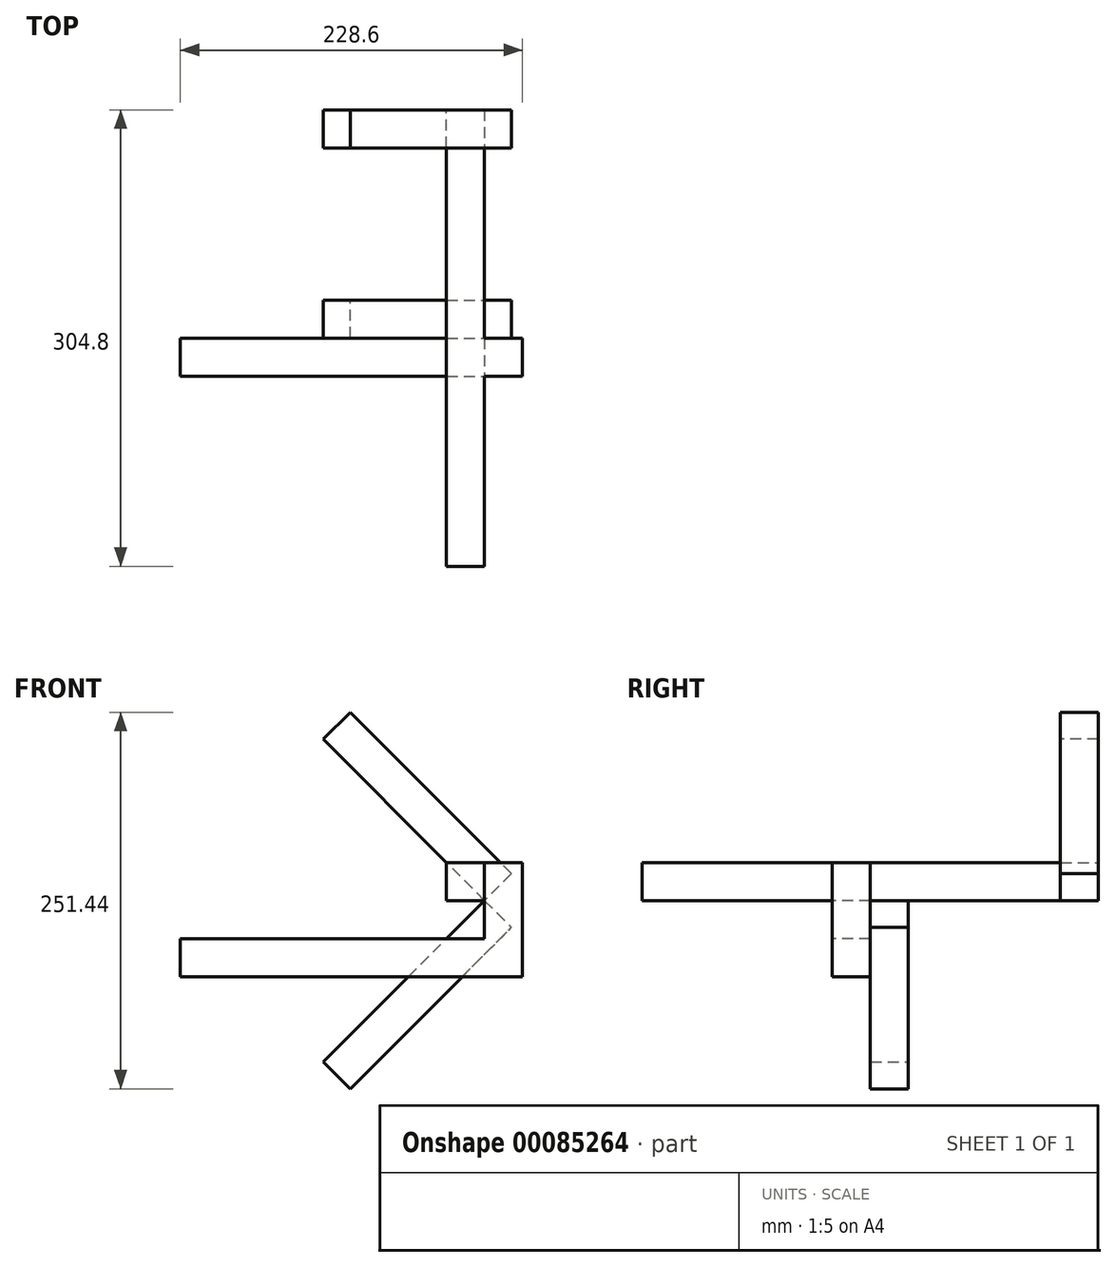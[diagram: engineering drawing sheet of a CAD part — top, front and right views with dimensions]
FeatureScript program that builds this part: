
annotation { "Feature Type Name" : "Feature", "Feature Type Description" : "" }
export const myFeature = defineFeature(function(context is Context, id is Id, definition is map)
    precondition{}
    {
        {
            var Q0;
            Q0=qCreatedBy(makeId("Front.planeOp"),FACE);
            var sketch = newSketch(context, id + "F0", { "sketchPlane" : qUnion([Q0])});
            skLineSegment(sketch, "E0.bottom", {"start": v(0, 0) * mm, "end": v(-25.4, 0) * mm});
            skLineSegment(sketch, "E0.top", {"start": v(0, 25.4) * mm, "end": v(-25.4, 25.4) * mm});
            skLineSegment(sketch, "E0.left", {"start": v(0, 0) * mm, "end": v(0, 25.4) * mm});
            skLineSegment(sketch, "E0.right", {"start": v(-25.4, 0) * mm, "end": v(-25.4, 25.4) * mm});
            skSolve(sketch);
        }
        {
            var Q0;
            Q0=makeQuery(id+"F0.imprint","IMPRINT",FACE,{"disambiguationData":[TD([[makeQuery(id+"F0.imprint","IMPRINT",EDGE,{"derivedFrom":sQuery(id+"F0.wireOp",EDGE,"E0.bottom")}),-1.0]])]});
            extrude(context, id + "F1", {"entities" : qUnion([Q0]), "endBound" : BoundingType.SYMMETRIC, "depth" : 304.8 * mm});
        }
        {
            var Q0;
            Q0=qCreatedBy(makeId("Top.planeOp"),FACE);
            var sketch = newSketch(context, id + "F2", { "sketchPlane" : qUnion([Q0])});
            skLineSegment(sketch, "E1.bottom", {"start": v(0, 0) * mm, "end": v(25.4, 0) * mm});
            skLineSegment(sketch, "E1.top", {"start": v(0, -25.4) * mm, "end": v(25.4, -25.4) * mm});
            skLineSegment(sketch, "E1.left", {"start": v(0, 0) * mm, "end": v(0, -25.4) * mm});
            skLineSegment(sketch, "E1.right", {"start": v(25.4, 0) * mm, "end": v(25.4, -25.4) * mm});
            skSolve(sketch);
        }
        {
            var Q0;
            Q0=makeQuery(id+"F2.imprint","IMPRINT",FACE,{"disambiguationData":[TD([[makeQuery(id+"F2.imprint","IMPRINT",EDGE,{"derivedFrom":sQuery(id+"F2.wireOp",EDGE,"E1.bottom")}),-1.0]])]});
            extrude(context, id + "F3", {"entities" : qUnion([Q0]), "operationType" : NewBodyOperationType.ADD, "depth" : 25.4 * mm});
        }
        {
            var Q0;
            Q0=makeQuery(id+"F2.imprint","IMPRINT",FACE,{"disambiguationData":[TD([[makeQuery(id+"F2.imprint","IMPRINT",EDGE,{"derivedFrom":sQuery(id+"F2.wireOp",EDGE,"E1.bottom")}),-1.0]])]});
            extrude(context, id + "F4", {"entities" : qUnion([Q0]), "operationType" : NewBodyOperationType.ADD, "oppositeDirection" : true, "depth" : 50.8 * mm});
        }
        {
            var Q0;
            Q0=qCreatedBy(makeId("Right.planeOp"),FACE);
            var sketch = newSketch(context, id + "F5", { "sketchPlane" : qUnion([Q0])});
            skLineSegment(sketch, "E2.0.0", {"start": v(-25.4, 0) * mm, "end": v(0, 0) * mm});
            skLineSegment(sketch, "E2.0.1", {"start": v(0, 0) * mm, "end": v(0, -50.8) * mm});
            skLineSegment(sketch, "E2.0.2", {"start": v(0, -50.8) * mm, "end": v(-25.4, -50.8) * mm});
            skLineSegment(sketch, "E2.0.3", {"start": v(-25.4, -50.8) * mm, "end": v(-25.4, 0) * mm});
            skLineSegment(sketch, "E3.top", {"start": v(0, -25.4) * mm, "end": v(-25.4, -25.4) * mm});
            skLineSegment(sketch, "E3.left", {"start": v(0, -50.8) * mm, "end": v(0, -25.4) * mm});
            skLineSegment(sketch, "E3.right", {"start": v(-25.4, -50.8) * mm, "end": v(-25.4, -25.4) * mm});
            skSolve(sketch);
        }
        {
            var Q0;
            Q0=makeQuery(id+"F5.imprint","IMPRINT",FACE,{"disambiguationData":[TD([[makeQuery(id+"F5.imprint","IMPRINT",EDGE,{"derivedFrom":sQuery(id+"F5.wireOp",EDGE,"E2.0.2")}),-1.0]])]});
            extrude(context, id + "F6", {"entities" : qUnion([Q0]), "operationType" : NewBodyOperationType.ADD, "oppositeDirection" : true, "depth" : 203.2 * mm});
        }
        {
            var Q0;
            Q0=qCreatedBy(makeId("Top.planeOp"),FACE);
            var sketch = newSketch(context, id + "F7", { "sketchPlane" : qUnion([Q0])});
            skLineSegment(sketch, "E4.bottom", {"start": v(0, 0) * mm, "end": v(25.4, 0) * mm});
            skLineSegment(sketch, "E4.top", {"start": v(0, 25.4) * mm, "end": v(25.4, 25.4) * mm});
            skLineSegment(sketch, "E4.left", {"start": v(0, 0) * mm, "end": v(0, 25.4) * mm});
            skLineSegment(sketch, "E4.right", {"start": v(25.4, 0) * mm, "end": v(25.4, 25.4) * mm});
            skSolve(sketch);
        }
        {
            var Q0;
            Q0=makeQuery(id+"F7.imprint","IMPRINT",FACE,{"disambiguationData":[TD([[makeQuery(id+"F7.imprint","IMPRINT",EDGE,{"derivedFrom":sQuery(id+"F7.wireOp",EDGE,"E4.bottom")}),1.0]])]});
            extrude(context, id + "F8", {"entities" : qUnion([Q0]), "oppositeDirection" : true, "depth" : 152.4 * mm});
        }
        {
            var Q0;
            Q0=makeQuery(id+"F8.opExtrude","SWEPT_BODY",BODY,{"disambiguationData":[OSD([sQuery(id+"F7.wireOp",EDGE,"E4.bottom"),sQuery(id+"F7.wireOp",EDGE,"E4.top"),sQuery(id+"F7.wireOp",EDGE,"E4.left"),sQuery(id+"F7.wireOp",EDGE,"E4.right")])]});
            var Q1;
            Q1=makeQuery(id+"F8.opExtrude","CAP_EDGE",EDGE,{"disambiguationData":[OSD([sQuery(id+"F7.wireOp",EDGE,"E4.left")])],"isStart":true});
            transform(context, id + "F9", {"entities" : qUnion([Q0]), "transformType" : TransformType.ROTATION, "transformAxis" : qUnion([Q1]), "angle" : 45 * degree, "makeCopy" : false});
        }
        {
            var Q0;
            Q0=makeQuery(id+"F8.opExtrude","SWEPT_FACE",FACE,{"disambiguationData":[OSD([sQuery(id+"F7.wireOp",EDGE,"E4.left")])]});
            cPlane(context, id + "F10", {"entities" : qUnion([Q0]), "cplaneType" : CPlaneType.OFFSET, "offset" : 152.4 * mm, "width" : 152.4 * mm, "height" : 152.4 * mm});
        }
        {
            var Q0;
            Q0=qCreatedBy(id+"F10.planeOp",FACE);
            var sketch = newSketch(context, id + "F11", { "sketchPlane" : qUnion([Q0])});
            skLineSegment(sketch, "E5.0.0", {"start": v(0, 0) * mm, "end": v(0, 25.4) * mm, "construction": true});
            skLineSegment(sketch, "E5.0.1", {"start": v(0, 25.4) * mm, "end": v(-152.4, 25.4) * mm, "construction": true});
            skLineSegment(sketch, "E5.0.2", {"start": v(-152.4, 25.4) * mm, "end": v(-152.4, 0) * mm, "construction": true});
            skLineSegment(sketch, "E5.0.3", {"start": v(-152.4, 0) * mm, "end": v(0, 0) * mm, "construction": true});
            skLineSegment(sketch, "E6.bottom", {"start": v(-152.4, 25.4) * mm, "end": v(-127, 25.4) * mm});
            skLineSegment(sketch, "E6.top", {"start": v(-152.4, 0) * mm, "end": v(-127, 0) * mm});
            skLineSegment(sketch, "E6.left", {"start": v(-152.4, 25.4) * mm, "end": v(-152.4, 0) * mm});
            skLineSegment(sketch, "E6.right", {"start": v(-127, 25.4) * mm, "end": v(-127, 0) * mm});
            skSolve(sketch);
        }
        {
            var Q0;
            Q0=makeQuery(id+"F11.imprint","IMPRINT",FACE,{"disambiguationData":[TD([[makeQuery(id+"F11.imprint","IMPRINT",EDGE,{"derivedFrom":sQuery(id+"F11.wireOp",EDGE,"E6.bottom")}),-1.0]])]});
            extrude(context, id + "F12", {"entities" : qUnion([Q0]), "oppositeDirection" : true, "depth" : 152.4 * mm});
        }
    });
